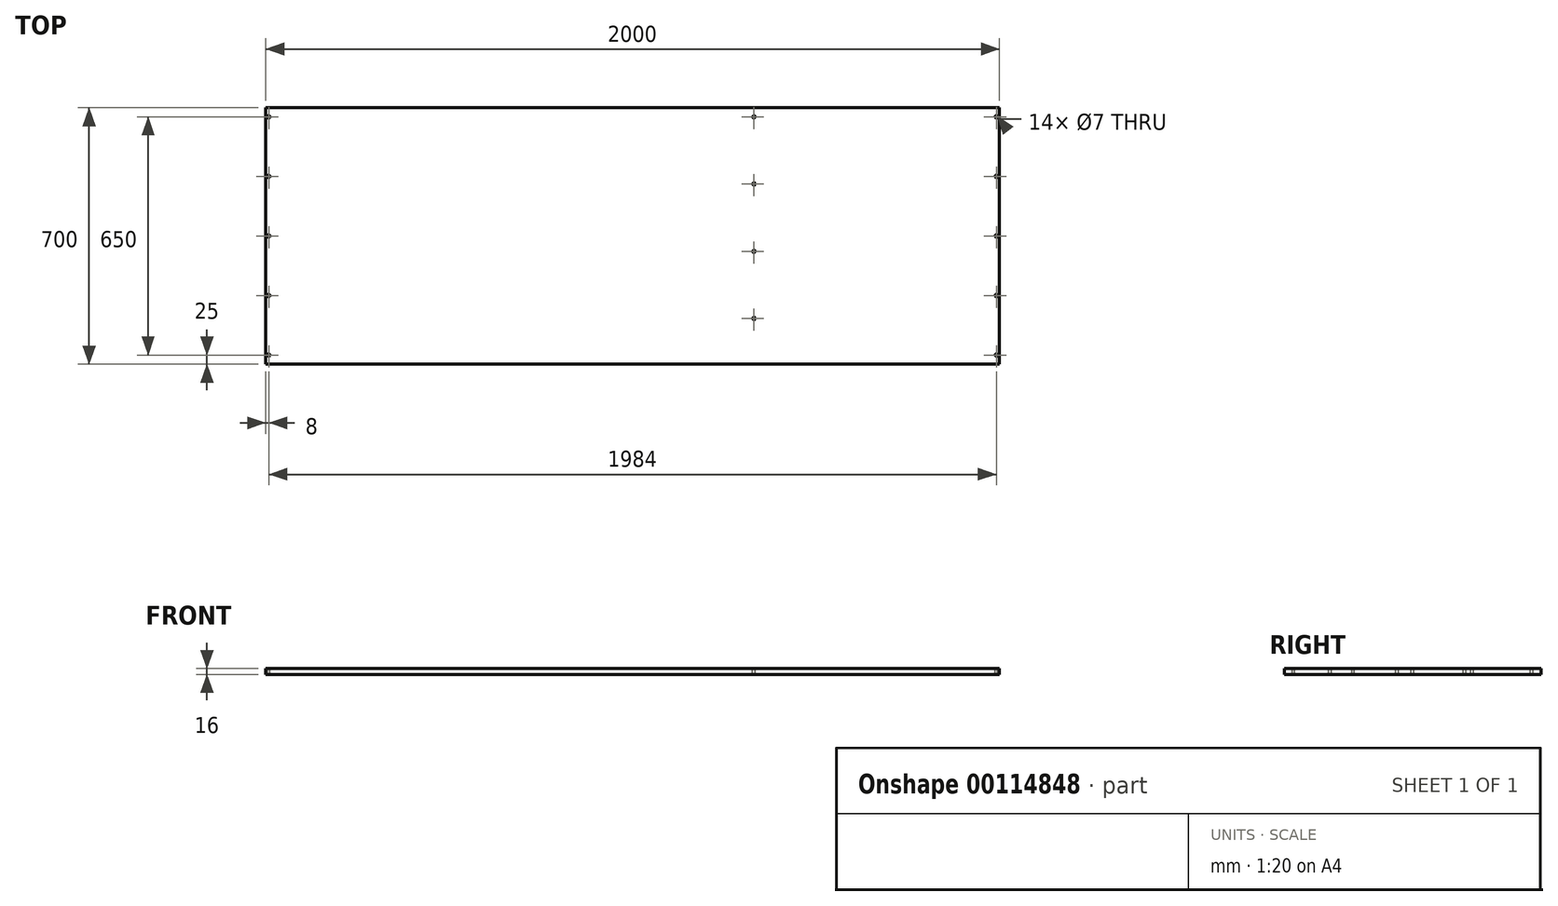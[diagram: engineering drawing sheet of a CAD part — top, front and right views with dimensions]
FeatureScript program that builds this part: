
annotation { "Feature Type Name" : "Feature", "Feature Type Description" : "" }
export const myFeature = defineFeature(function(context is Context, id is Id, definition is map)
    precondition{}
    {
        {
            var Q0;
            Q0=qCreatedBy(makeId("Top.planeOp"),FACE);
            var sketch = newSketch(context, id + "F0", { "sketchPlane" : qUnion([Q0])});
            skLineSegment(sketch, "E0.bottom", {"start": v(-1000, 350) * mm, "end": v(1000, 350) * mm});
            skLineSegment(sketch, "E0.top", {"start": v(-1000, -350) * mm, "end": v(1000, -350) * mm});
            skLineSegment(sketch, "E0.left", {"start": v(-1000, 350) * mm, "end": v(-1000, -350) * mm});
            skLineSegment(sketch, "E0.right", {"start": v(1000, 350) * mm, "end": v(1000, -350) * mm});
            skPoint(sketch, "E0.middle", {"position": v(0, 0) * mm});
            skSolve(sketch);
        }
        {
            var Q0;
            Q0=makeQuery(id+"F0.imprint","IMPRINT",FACE,{"disambiguationData":[TD([[makeQuery(id+"F0.imprint","IMPRINT",EDGE,{"derivedFrom":sQuery(id+"F0.wireOp",EDGE,"E0.bottom")}),-1.0]])]});
            extrude(context, id + "F1", {"entities" : qUnion([Q0]), "endBound" : BoundingType.SYMMETRIC, "depth" : 16 * mm});
        }
        {
            var Q0;
            Q0=makeQuery(id+"F1.opExtrude","CAP_FACE",FACE,{"disambiguationData":[OSD([sQuery(id+"F0.wireOp",EDGE,"E0.bottom"),sQuery(id+"F0.wireOp",EDGE,"E0.top"),sQuery(id+"F0.wireOp",EDGE,"E0.left"),sQuery(id+"F0.wireOp",EDGE,"E0.right")])],"isStart":false});
            var sketch = newSketch(context, id + "F2", { "sketchPlane" : qUnion([Q0])});
            skPoint(sketch, "E1", {"position": v(-992, 325) * mm});
            skPoint(sketch, "E2", {"position": v(-992, 162.5) * mm});
            skPoint(sketch, "E3", {"position": v(-992, 0) * mm});
            skPoint(sketch, "E4.MirrorP", {"position": v(-992, -325) * mm});
            skPoint(sketch, "E5.MirrorP", {"position": v(-992, -162.5) * mm});
            skPoint(sketch, "E6.MirrorP", {"position": v(992, -162.5) * mm});
            skPoint(sketch, "E7.MirrorP", {"position": v(992, -325) * mm});
            skPoint(sketch, "E8.MirrorP", {"position": v(992, 325) * mm});
            skPoint(sketch, "E9.MirrorP", {"position": v(992, 0) * mm});
            skPoint(sketch, "E10.MirrorP", {"position": v(992, 162.5) * mm});
            skPoint(sketch, "E11", {"position": v(331, 325) * mm});
            skPoint(sketch, "E12", {"position": v(331, -225) * mm});
            skPoint(sketch, "E13", {"position": v(331, 142) * mm});
            skPoint(sketch, "E14", {"position": v(331, -42) * mm});
            skSolve(sketch);
        }
        {
            var Q0;
            Q0=sQuery(id+"F2.wireOp",VERTEX,"E1");
            var Q1;
            Q1=sQuery(id+"F2.wireOp",VERTEX,"E2");
            var Q2;
            Q2=sQuery(id+"F2.wireOp",VERTEX,"E3");
            var Q3;
            Q3=sQuery(id+"F2.wireOp",VERTEX,"E5.MirrorP");
            var Q4;
            Q4=sQuery(id+"F2.wireOp",VERTEX,"E4.MirrorP");
            var Q5;
            Q5=sQuery(id+"F2.wireOp",VERTEX,"E8.MirrorP");
            var Q6;
            Q6=sQuery(id+"F2.wireOp",VERTEX,"E10.MirrorP");
            var Q7;
            Q7=sQuery(id+"F2.wireOp",VERTEX,"E9.MirrorP");
            var Q8;
            Q8=sQuery(id+"F2.wireOp",VERTEX,"E6.MirrorP");
            var Q9;
            Q9=sQuery(id+"F2.wireOp",VERTEX,"E7.MirrorP");
            var Q10;
            Q10=sQuery(id+"F2.wireOp",VERTEX,"E12");
            var Q11;
            Q11=sQuery(id+"F2.wireOp",VERTEX,"E14");
            var Q12;
            Q12=sQuery(id+"F2.wireOp",VERTEX,"E13");
            var Q13;
            Q13=sQuery(id+"F2.wireOp",VERTEX,"E11");
            var Q14;
            Q14=makeQuery(id+"F1.opExtrude","SWEPT_BODY",BODY,{"disambiguationData":[OSD([sQuery(id+"F0.wireOp",EDGE,"E0.bottom"),sQuery(id+"F0.wireOp",EDGE,"E0.top"),sQuery(id+"F0.wireOp",EDGE,"E0.left"),sQuery(id+"F0.wireOp",EDGE,"E0.right")])]});
            hole(context, id + "F3", {"style" : HoleStyle.SIMPLE, "endStyle" : HoleEndStyle.THROUGH, "holeDiameter" : 7 * mm, "locations" : qUnion([Q0, Q1, Q2, Q3, Q4, Q5, Q6, Q7, Q8, Q9, Q10, Q11, Q12, Q13]), "scope" : qUnion([Q14]), "isTappedThrough" : true});
        }
    });
